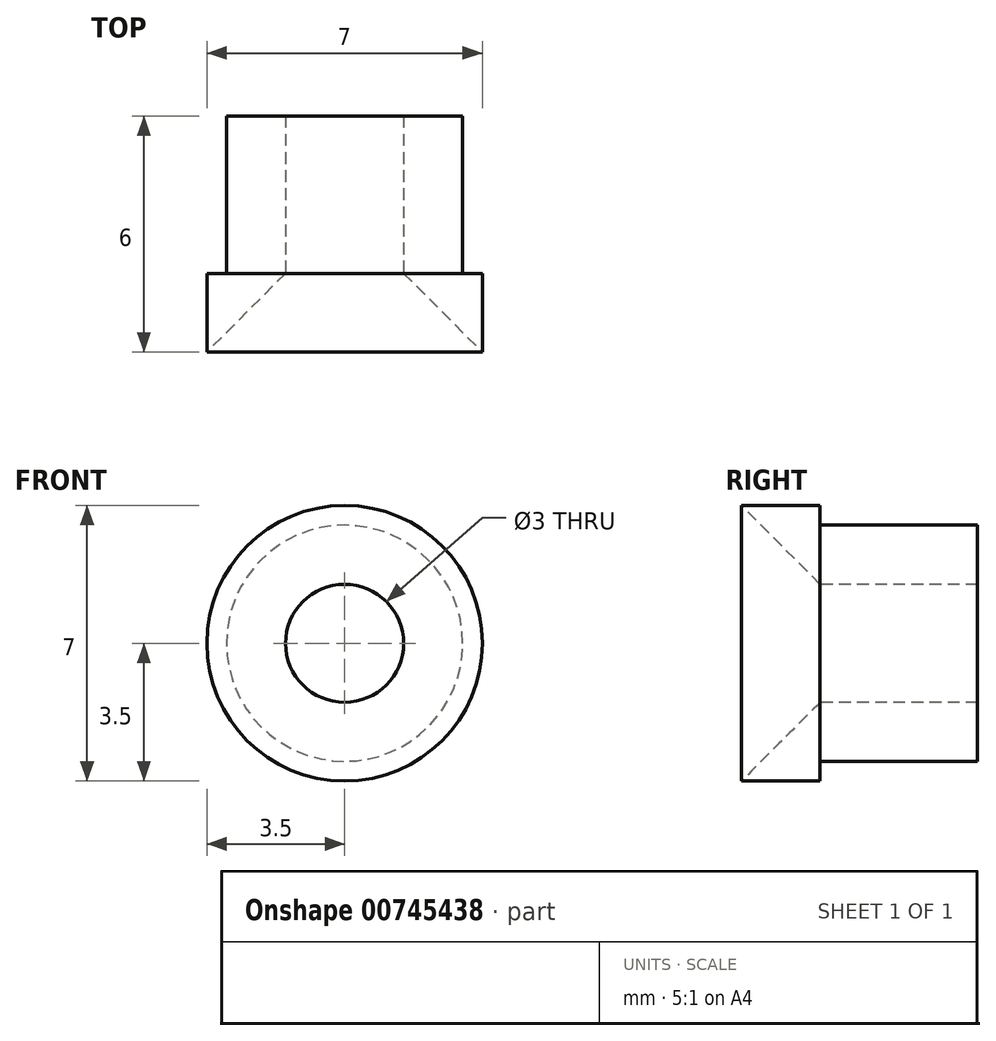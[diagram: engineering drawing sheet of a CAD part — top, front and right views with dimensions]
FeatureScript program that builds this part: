
annotation { "Feature Type Name" : "Feature", "Feature Type Description" : "" }
export const myFeature = defineFeature(function(context is Context, id is Id, definition is map)
    precondition{}
    {
        {
            var Q0;
            Q0=qCreatedBy(makeId("Front.planeOp"),FACE);
            var sketch = newSketch(context, id + "F0", { "sketchPlane" : qUnion([Q0])});
            skCircle(sketch, "E0", {"center": v(0, 0) * mm, "radius": 3.5 * mm});
            skCircle(sketch, "E1", {"center": v(0, 0) * mm, "radius": 1.5 * mm});
            skSolve(sketch);
        }
        {
            var Q0;
            Q0=makeQuery(id+"F0.imprint","IMPRINT",FACE,{"disambiguationData":[TD([[makeQuery(id+"F0.imprint","IMPRINT",EDGE,{"derivedFrom":sQuery(id+"F0.wireOp",EDGE,"E0")}),1.0]])]});
            extrude(context, id + "F1", {"entities" : qUnion([Q0]), "depth" : 2 * mm, "offsetDistance" : 25 * mm});
        }
        {
            var Q0;
            Q0=makeQuery(id+"F1.opExtrude","CAP_EDGE",EDGE,{"disambiguationData":[OSD([sQuery(id+"F0.wireOp",EDGE,"E1")])],"isStart":false});
            chamfer(context, id + "F2", {"entities" : qUnion([Q0]), "width" : 2 * mm, "tangentPropagation" : true});
        }
        {
            var Q0;
            Q0=makeQuery(id+"F1.opExtrude","CAP_FACE",FACE,{"disambiguationData":[OSD([sQuery(id+"F0.wireOp",EDGE,"E0"),sQuery(id+"F0.wireOp",EDGE,"E1")])],"isStart":true});
            var sketch = newSketch(context, id + "F3", { "sketchPlane" : qUnion([Q0])});
            skCircle(sketch, "E2", {"center": v(0, 0) * mm, "radius": 3 * mm});
            skCircle(sketch, "E3", {"center": v(0, 0) * mm, "radius": 1.5 * mm});
            skSolve(sketch);
        }
        {
            var Q0;
            Q0=makeQuery(id+"F3.imprint","IMPRINT",FACE,{"disambiguationData":[TD([[makeQuery(id+"F3.imprint","IMPRINT",EDGE,{"derivedFrom":sQuery(id+"F3.wireOp",EDGE,"E2")}),1.0]])]});
            extrude(context, id + "F4", {"entities" : qUnion([Q0]), "operationType" : NewBodyOperationType.ADD, "depth" : 4 * mm, "offsetDistance" : 25 * mm});
        }
    });
